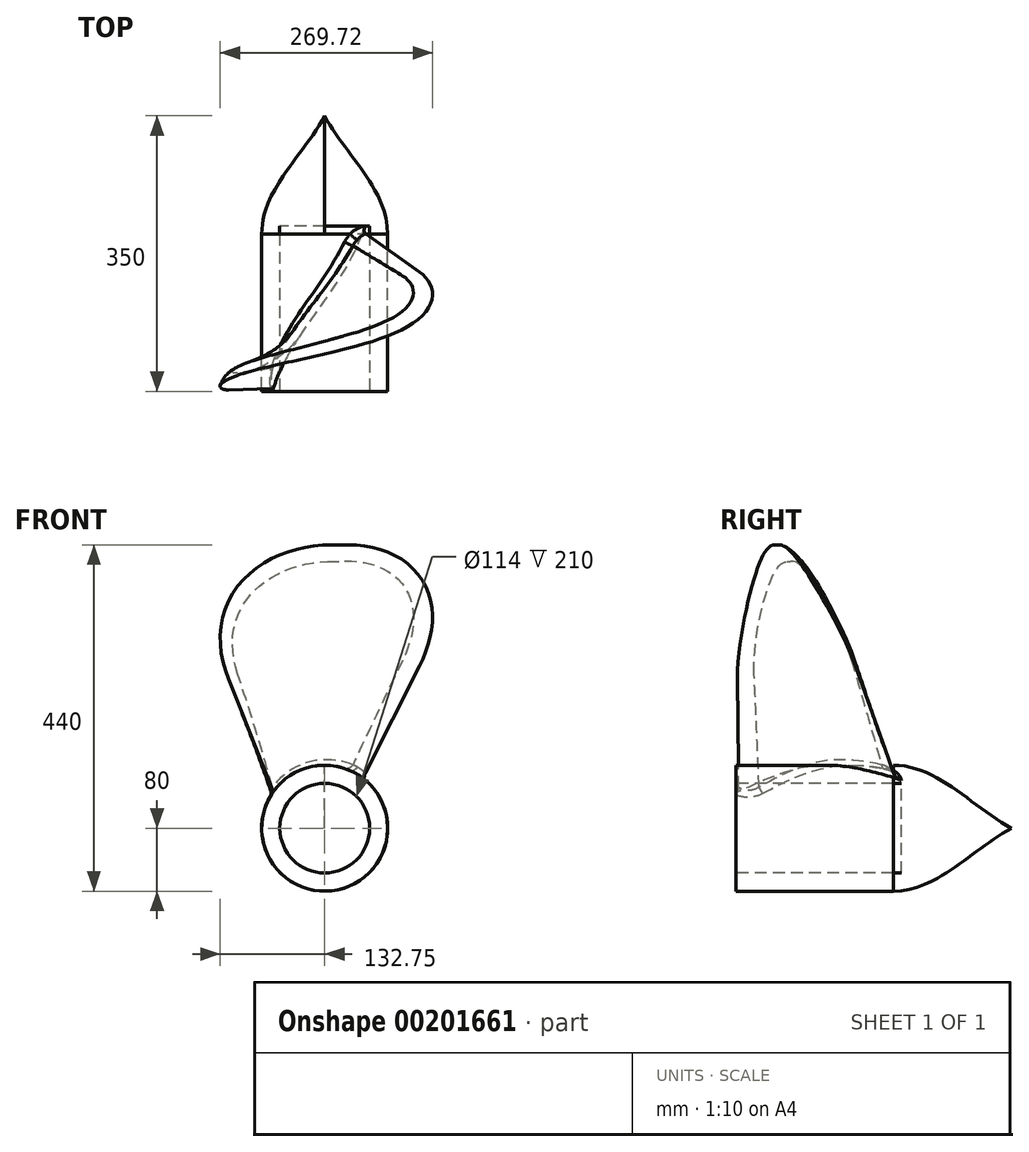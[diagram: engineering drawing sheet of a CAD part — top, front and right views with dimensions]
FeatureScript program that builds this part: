
annotation { "Feature Type Name" : "Feature", "Feature Type Description" : "" }
export const myFeature = defineFeature(function(context is Context, id is Id, definition is map)
    precondition{}
    {
        {
            var Q0;
            Q0=qCreatedBy(makeId("Right.planeOp"),FACE);
            var sketch = newSketch(context, id + "F0", { "sketchPlane" : qUnion([Q0])});
            skLineSegment(sketch, "E0", {"start": v(0, 0) * mm, "end": v(-350, 0) * mm});
            skLineSegment(sketch, "E1", {"start": v(-350, 0) * mm, "end": v(-350, 80) * mm});
            skLineSegment(sketch, "E2", {"start": v(-350, 80) * mm, "end": v(-150, 80) * mm});
            skFitSpline(sketch, "E3", {"points": [v(0, 0) * mm, v(-150, 80) * mm], "startDerivative": vector(-150, 80) * mm, "endDerivative": vector(-170, 0) * mm});
            skSolve(sketch);
        }
        {
            var Q0;
            Q0=makeQuery(id+"F0.imprint","IMPRINT",FACE,{"disambiguationData":[TD([[makeQuery(id+"F0.imprint","IMPRINT",EDGE,{"derivedFrom":sQuery(id+"F0.wireOp",EDGE,"E0")}),-1.0]])]});
            var Q1;
            Q1=sQuery(id+"F0.wireOp",EDGE,"E0");
            revolve(context, id + "F1", {"entities" : qUnion([Q0]), "axis" : qUnion([Q1]), "revolveType" : RevolveType.FULL});
        }
        {
            var Q0;
            Q0=qCreatedBy(makeId("Top.planeOp"),FACE);
            var sketch = newSketch(context, id + "F2", { "sketchPlane" : qUnion([Q0])});
            skLineSegment(sketch, "E4.bottom", {"start": v(-58.54, -342.78) * mm, "end": v(-47, -346.1) * mm});
            skLineSegment(sketch, "E4.top", {"start": v(4.86, -121.7) * mm, "end": v(16.4, -125) * mm});
            skLineSegment(sketch, "E4.left", {"start": v(-58.54, -342.78) * mm, "end": v(4.86, -121.7) * mm});
            skLineSegment(sketch, "E4.right", {"start": v(-47, -346.1) * mm, "end": v(16.4, -125) * mm});
            skLineSegment(sketch, "E5", {"start": v(0, 0) * mm, "end": v(0, -513.39) * mm, "construction": true});
            skSolve(sketch);
        }
        {
            var Q0;
            Q0=qCreatedBy(makeId("Top.planeOp"),FACE);
            cPlane(context, id + "F3", {"entities" : qUnion([Q0]), "cplaneType" : CPlaneType.OFFSET, "offset" : 360 * mm, "width" : 150 * mm, "height" : 150 * mm});
        }
        {
            var Q0;
            Q0=qCreatedBy(id+"F3.planeOp",FACE);
            var sketch = newSketch(context, id + "F4", { "sketchPlane" : qUnion([Q0])});
            skLineSegment(sketch, "E6.bottom", {"start": v(-190, -350) * mm, "end": v(-192.9, -338.36) * mm});
            skLineSegment(sketch, "E6.top", {"start": v(198.12, -253.23) * mm, "end": v(195.22, -241.59) * mm});
            skLineSegment(sketch, "E6.left", {"start": v(-190, -350) * mm, "end": v(198.12, -253.23) * mm});
            skLineSegment(sketch, "E6.right", {"start": v(-192.9, -338.36) * mm, "end": v(195.22, -241.59) * mm});
            skSolve(sketch);
        }
        {
            var Q1;
            Q1=qSketchRegion(id+"F2",true);
            var Q2;
            Q2=qSketchRegion(id+"F4",true);
            loft(context, id + "F5", {"operationType" : NewBodyOperationType.ADD, "sheetProfilesArray" : [{ "sheetProfileEntities" : qUnion([Q1]) }, { "sheetProfileEntities" : qUnion([Q2]) }]});
        }
        {
            var Q0;
            Q0=makeQuery(id+"F5.opLoft","MID_CAP_EDGE",EDGE,{"disambiguationData":[OSD([sQuery(id+"F4.wireOp",EDGE,"E6.top"),sQuery(id+"F4.wireOp",EDGE,"E6.left"),sQuery(id+"F4.wireOp",EDGE,"E6.right")])],"capPos":1.0});
            var Q1;
            Q1=makeQuery(id+"F5.opLoft","MID_CAP_EDGE",EDGE,{"disambiguationData":[OSD([sQuery(id+"F4.wireOp",EDGE,"E6.bottom"),sQuery(id+"F4.wireOp",EDGE,"E6.left"),sQuery(id+"F4.wireOp",EDGE,"E6.right")])],"capPos":1.0});
            fillet(context, id + "F6", {"entities" : qUnion([Q0, Q1]), "radius" : 132.5 * mm, "tangentPropagation" : true, "allowEdgeOverflow" : false});
        }
        {
            var Q0;
            Q0=makeQuery(id+"F5.opLoft","SWEPT_EDGE",EDGE,{"disambiguationData":[OSD([sQuery(id+"F2.wireOp",EDGE,"E4.top"),sQuery(id+"F2.wireOp",EDGE,"E4.left"),sQuery(id+"F4.wireOp",EDGE,"E6.top"),sQuery(id+"F4.wireOp",EDGE,"E6.right")])]});
            fillet(context, id + "F7", {"entities" : qUnion([Q0]), "radius" : 30 * mm, "tangentPropagation" : true, "allowEdgeOverflow" : false});
        }
        {
            var Q0;
            Q0=makeQuery(id+"F5.boolean.opBoolean","INTERSECT",EDGE,{"derivedFrom":[makeQuery(id+"F1.opRevolve","SWEPT_FACE",FACE,{"disambiguationData":[OSD([sQuery(id+"F0.wireOp",EDGE,"E2")])]}),makeQuery(id+"F5.opLoft","SWEPT_FACE",FACE,{"disambiguationData":[OSD([sQuery(id+"F2.wireOp",EDGE,"E4.bottom"),sQuery(id+"F2.wireOp",EDGE,"E4.top"),sQuery(id+"F2.wireOp",EDGE,"E4.left"),sQuery(id+"F4.wireOp",EDGE,"E6.bottom"),sQuery(id+"F4.wireOp",EDGE,"E6.top"),sQuery(id+"F4.wireOp",EDGE,"E6.right")])]})]});
            fillet(context, id + "F8", {"entities" : qUnion([Q0]), "radius" : 10 * mm, "tangentPropagation" : true, "allowEdgeOverflow" : false});
        }
        {
            var Q0;
            Q0=makeQuery(id+"F1.opRevolve","SWEPT_FACE",FACE,{"disambiguationData":[OSD([sQuery(id+"F0.wireOp",EDGE,"E1")])]});
            var sketch = newSketch(context, id + "F9", { "sketchPlane" : qUnion([Q0])});
            skCircle(sketch, "E7", {"center": v(0, 0) * mm, "radius": 57 * mm});
            skSolve(sketch);
        }
        {
            var Q0;
            Q0=makeQuery(id+"F9.imprint","IMPRINT",FACE,{"disambiguationData":[TD([[makeQuery(id+"F9.imprint","IMPRINT",EDGE,{"derivedFrom":sQuery(id+"F9.wireOp",EDGE,"E7")}),1.0]])]});
            extrude(context, id + "F10", {"entities" : qUnion([Q0]), "operationType" : NewBodyOperationType.REMOVE, "oppositeDirection" : true, "depth" : 210 * mm});
        }
    });
